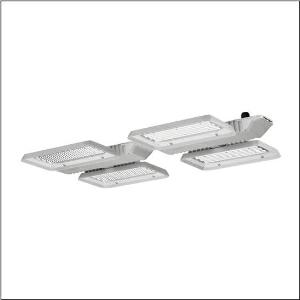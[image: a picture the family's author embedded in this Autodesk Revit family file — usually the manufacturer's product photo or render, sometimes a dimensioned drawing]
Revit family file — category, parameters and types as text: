
# Revit family: highbay_11_51hla2d24nca
name_source: partatom
category: Lighting Fixtures
units: mm (PartAtom-declared; Revit-internal decimal feet)

## family parameters
Cut with Voids When Loaded = No
Host = Face
Light Source = No
Part Type = Normal
Room Calculation Point = No
Round Connector Dimension = Use Diameter
Shared = No

## types (1)
- --- (1 x LED, 33150 lm, 189.6 W, 4000K)
    Apparent Load = 190 VA
    CIE Flux Codes = 89 96 99 100 100
    Color Rendering = 80
    Color Temperature = 4000K
    Default Elevation = 1800 mm
    Description = Highbay 11, LED high bay luminaire, primary light control with lens, of PMMA, light emission: direct distribution, primary light characteristic: symmetric, installation type: surface-mounted, suspended mounting, for 2x 2x LED, rated luminous flux: 33.150lm, luminous efficacy: 175lm/W, light colour: 840, colour temperature: 4000K, control gear: ECG DALI, with terminal, 5-pole, max. 2.5mm², mains connection: 230..240V, AC, 50/60Hz, rated input power: 190W, LED unit, of diecast aluminium, unplated, bead blasted, silver, length: 940mm, width: 500mm, height: 65mm, housing, of diecast aluminium, uncoated, bead blasted, silver, protection rating (complete): IP65, insulation class (complete): insulation class I (protective earthing), certification: CE, ENEC, VDE, UKCA, protection symbol: D, impact resistance: IK08 with glass or PC cover, permissible operating ambient temperature: -35..+45°C, reducing of maximum allowable ambient temperature of 5°C with ceiling mounting, corresponds to IFS (International Featured Standards) requirements for safety and quality in the food industry, packaging unit: 1 piece
    Height = 95 mm
    Lamp = 1 x LED
    Lamp Light Flux = 33150 lm
    Lamp Power = 189.6 W
    Lamp count = 1
    Length = 939 mm
    Luminous efficacy = 175 lm/W
    Manufacturer = Siteco
    ModVariant = No
    Model = 51HLA2D24NCA
    Mounting Place = Ceiling
    Mounting Type = Pendant
    Number of Poles = 1
    OnlyDefault = Yes
    Power Factor = 1
    Product Name = Highbay 11
    Product group = LED high bay luminaire
    ProductGroupID = 903
    Protection Class = Protection class I
    Protection Degree = IP 65
    RLX_Detail_Level = 1
    RLX_Emergency_Light_Flux = 0 lm
    RLX_Emergency_Type = 0
    RLX_Emergency_Type_DB = No
    RlxData = <blob elided: 97117 chars, md5=2e13d308>
    Socket = socket
    Standby Power = 0 W
    System Light Flux = 33150 lm
    System Power = 190 W
    Type Comments = factory setting: luminous flux: 100 % | dim-lin: 254 | 535 mA
    Type Image = l_1003428.jpg
    URL = http://relux.com
    VarID = @adj_160027
    Voltage = 0 V
    Weight = 0.00 kg
    Width = 501 mm

## geometry (parser evidence)
native form markers: Blend x4, Sweep x14
no freeform markers — native parametric forms only
